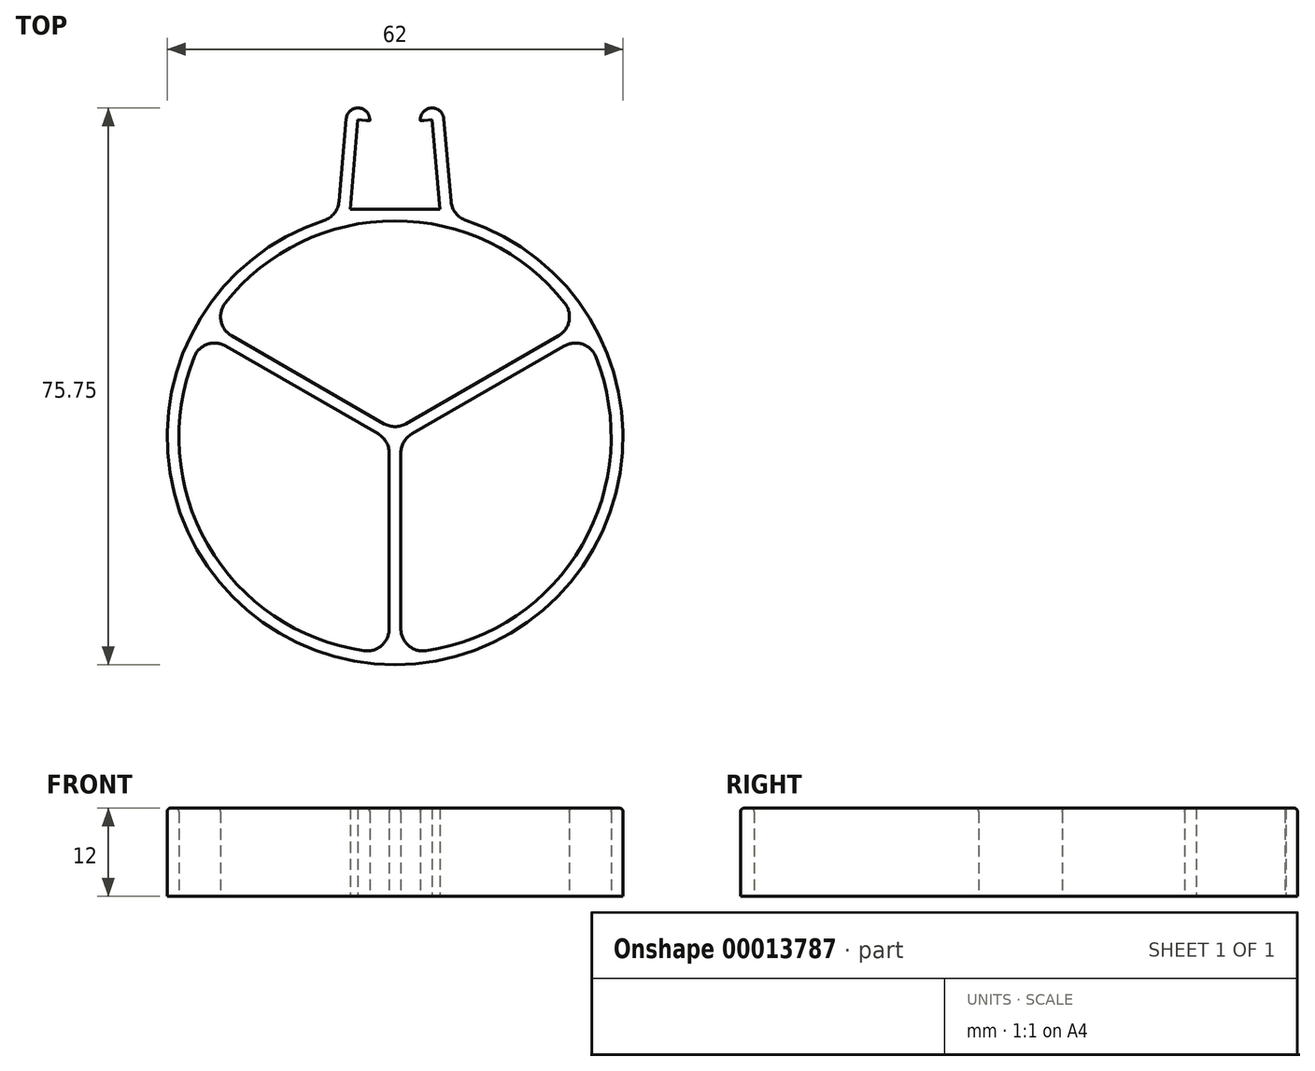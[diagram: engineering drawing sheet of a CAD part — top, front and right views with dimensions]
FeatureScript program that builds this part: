
annotation { "Feature Type Name" : "Feature", "Feature Type Description" : "" }
export const myFeature = defineFeature(function(context is Context, id is Id, definition is map)
    precondition{}
    {
        {
            var Q0;
            Q0=qCreatedBy(makeId("Top.planeOp"),FACE);
            var sketch = newSketch(context, id + "F0", { "sketchPlane" : qUnion([Q0])});
            skLineSegment(sketch, "E0.rect.bottom", {"start": v(6.1, 6.1) * mm, "end": v(-6.1, 6.1) * mm, "construction": true});
            skLineSegment(sketch, "E0.rect.top", {"start": v(6.1, -6.1) * mm, "end": v(-6.1, -6.1) * mm, "construction": true});
            skLineSegment(sketch, "E0.rect.left", {"start": v(6.1, 6.1) * mm, "end": v(6.1, -6.1) * mm, "construction": true});
            skLineSegment(sketch, "E0.rect.right", {"start": v(-6.1, 6.1) * mm, "end": v(-6.1, -6.1) * mm, "construction": true});
            skPoint(sketch, "E0.rect.middle", {"position": v(0, 0) * mm});
            skLineSegment(sketch, "E1", {"start": v(-6.1, -6.1) * mm, "end": v(-5.04, 6.05) * mm});
            skLineSegment(sketch, "E2", {"start": v(0, 6.1) * mm, "end": v(0, -66.5) * mm, "construction": true});
            skLineSegment(sketch, "E3", {"start": v(-6.1, -6.1) * mm, "end": v(6.1, -6.1) * mm});
            skLineSegment(sketch, "E4.1", {"start": v(-7.61, -5.06) * mm, "end": v(-6.63, 6.2) * mm});
            skLineSegment(sketch, "E5.0.MirrorCS", {"start": v(7.61, -5.06) * mm, "end": v(6.63, 6.2) * mm});
            skLineSegment(sketch, "E5.2.MirrorCS", {"start": v(6.1, -6.1) * mm, "end": v(5.04, 6.05) * mm});
            skArc(sketch, "E6", {"start": v(-9.67, -7.65) * mm, "mid": v(0, -68.1) * mm, "end": v(9.67, -7.65) * mm});
            skPoint(sketch, "E7.orphan", {"position": v(0, -6.1) * mm});
            skPoint(sketch, "E8.visualSharp", {"position": v(-7.8, -7.1) * mm});
            skArc(sketch, "E8.filletArc", {"start": v(-9.67, -7.65) * mm, "mid": v(-8.25, -6.66) * mm, "end": v(-7.61, -5.06) * mm});
            skPoint(sketch, "E9.visualSharp", {"position": v(7.8, -7.1) * mm});
            skArc(sketch, "E9.filletArc", {"start": v(7.61, -5.06) * mm, "mid": v(8.25, -6.66) * mm, "end": v(9.67, -7.65) * mm});
            skArc(sketch, "E10", {"start": v(-3.44, 5.91) * mm, "mid": v(-4.9, 7.65) * mm, "end": v(-6.63, 6.2) * mm});
            skLineSegment(sketch, "E11", {"start": v(-5.04, 6.05) * mm, "end": v(-3.44, 5.91) * mm});
            skArc(sketch, "E12", {"start": v(-5.04, 6.05) * mm, "mid": v(-5.57, 6.09) * mm, "end": v(-6.1, 6.1) * mm, "construction": true});
            skArc(sketch, "E13.0.MirrorCS", {"start": v(5.04, 6.05) * mm, "mid": v(5.57, 6.09) * mm, "end": v(6.1, 6.1) * mm, "construction": true});
            skLineSegment(sketch, "E14.0.MirrorCS", {"start": v(5.04, 6.05) * mm, "end": v(3.44, 5.91) * mm});
            skArc(sketch, "E15.0.MirrorCS", {"start": v(3.44, 5.91) * mm, "mid": v(4.9, 7.65) * mm, "end": v(6.63, 6.2) * mm});
            skArc(sketch, "E16.converted", {"start": v(4.23, -66.2) * mm, "mid": v(25.46, -51.8) * mm, "end": v(27.31, -26.22) * mm});
            skLineSegment(sketch, "E17", {"start": v(-0.8, -39.3) * mm, "end": v(-0.8, -63.23) * mm});
            skLineSegment(sketch, "E18.0.MirrorCS", {"start": v(0.8, -39.3) * mm, "end": v(0.8, -63.23) * mm});
            skPoint(sketch, "E19.visualSharp", {"position": v(0.8, -66.49) * mm});
            skArc(sketch, "E19.filletArc", {"start": v(0.8, -63.23) * mm, "mid": v(1.84, -65.5) * mm, "end": v(4.23, -66.2) * mm});
            skPoint(sketch, "E20.visualSharp", {"position": v(-0.8, -66.49) * mm});
            skArc(sketch, "E20.filletArc", {"start": v(-4.23, -66.2) * mm, "mid": v(-1.84, -65.5) * mm, "end": v(-0.8, -63.23) * mm});
            skLineSegment(sketch, "E21.1.1", {"start": v(2.3, -36.7) * mm, "end": v(23.02, -24.73) * mm});
            skLineSegment(sketch, "E21.1.2", {"start": v(1.5, -35.31) * mm, "end": v(22.22, -23.34) * mm});
            skArc(sketch, "E21.1.3", {"start": v(22.22, -23.34) * mm, "mid": v(23.67, -21.31) * mm, "end": v(23.08, -18.89) * mm});
            skArc(sketch, "E21.1.4", {"start": v(27.31, -26.22) * mm, "mid": v(25.5, -24.5) * mm, "end": v(23.02, -24.73) * mm});
            skLineSegment(sketch, "E21.2.1", {"start": v(-1.5, -35.31) * mm, "end": v(-22.22, -23.34) * mm});
            skLineSegment(sketch, "E21.2.2", {"start": v(-2.3, -36.7) * mm, "end": v(-23.02, -24.73) * mm});
            skArc(sketch, "E21.2.3", {"start": v(-23.02, -24.73) * mm, "mid": v(-25.5, -24.5) * mm, "end": v(-27.31, -26.22) * mm});
            skArc(sketch, "E21.2.4", {"start": v(-23.08, -18.89) * mm, "mid": v(-23.67, -21.31) * mm, "end": v(-22.22, -23.34) * mm});
            skPoint(sketch, "E22.newPointA", {"position": v(0.8, -37.1) * mm});
            skPoint(sketch, "E22.newPointB", {"position": v(0.4, -37.8) * mm});
            skArc(sketch, "E22.filletArc", {"start": v(2.3, -36.7) * mm, "mid": v(1.2, -37.8) * mm, "end": v(0.8, -39.3) * mm});
            skPoint(sketch, "E23.newPointA", {"position": v(0.4, -36.4) * mm});
            skPoint(sketch, "E23.newPointB", {"position": v(-0.4, -36.4) * mm});
            skArc(sketch, "E23.filletArc", {"start": v(-1.5, -35.31) * mm, "mid": v(0, -35.71) * mm, "end": v(1.5, -35.31) * mm});
            skPoint(sketch, "E24.newPointA", {"position": v(-0.4, -37.8) * mm});
            skPoint(sketch, "E24.newPointB", {"position": v(-0.8, -37.1) * mm});
            skArc(sketch, "E24.filletArc", {"start": v(-0.8, -39.3) * mm, "mid": v(-1.2, -37.8) * mm, "end": v(-2.3, -36.7) * mm});
            skArc(sketch, "E25.trimOffspring", {"start": v(23.08, -18.89) * mm, "mid": v(0, -7.7) * mm, "end": v(-23.08, -18.89) * mm});
            skArc(sketch, "E26.trimOffspring", {"start": v(-27.31, -26.22) * mm, "mid": v(-25.46, -51.8) * mm, "end": v(-4.23, -66.2) * mm});
            skSolve(sketch);
        }
        {
            var Q0;
            Q0=makeQuery(id+"F0.imprint","IMPRINT",FACE,{"disambiguationData":[TD([[makeQuery(id+"F0.imprint","IMPRINT",EDGE,{"derivedFrom":sQuery(id+"F0.wireOp",EDGE,"E1")}),1.0]])]});
            extrude(context, id + "F1", {"entities" : qUnion([Q0]), "depth" : 12 * mm});
        }
        {
            var Q0;
            Q0=makeQuery(id+"F1.opExtrude","CAP_EDGE",EDGE,{"disambiguationData":[OSD([sQuery(id+"F0.wireOp",EDGE,"E25.trimOffspring")])],"isStart":false});
            var Q1;
            Q1=makeQuery(id+"F1.opExtrude","CAP_EDGE",EDGE,{"disambiguationData":[OSD([sQuery(id+"F0.wireOp",EDGE,"E26.trimOffspring")])],"isStart":false});
            var Q2;
            Q2=makeQuery(id+"F1.opExtrude","CAP_EDGE",EDGE,{"disambiguationData":[OSD([sQuery(id+"F0.wireOp",EDGE,"E16.converted")])],"isStart":false});
            var Q3;
            Q3=makeQuery(id+"F1.opExtrude","CAP_EDGE",EDGE,{"disambiguationData":[OSD([sQuery(id+"F0.wireOp",EDGE,"E6")])],"isStart":false});
            fillet(context, id + "F2", {"entities" : qUnion([Q0, Q1, Q2, Q3]), "radius" : 0.5 * mm, "tangentPropagation" : true, "allowEdgeOverflow" : false});
        }
    });
